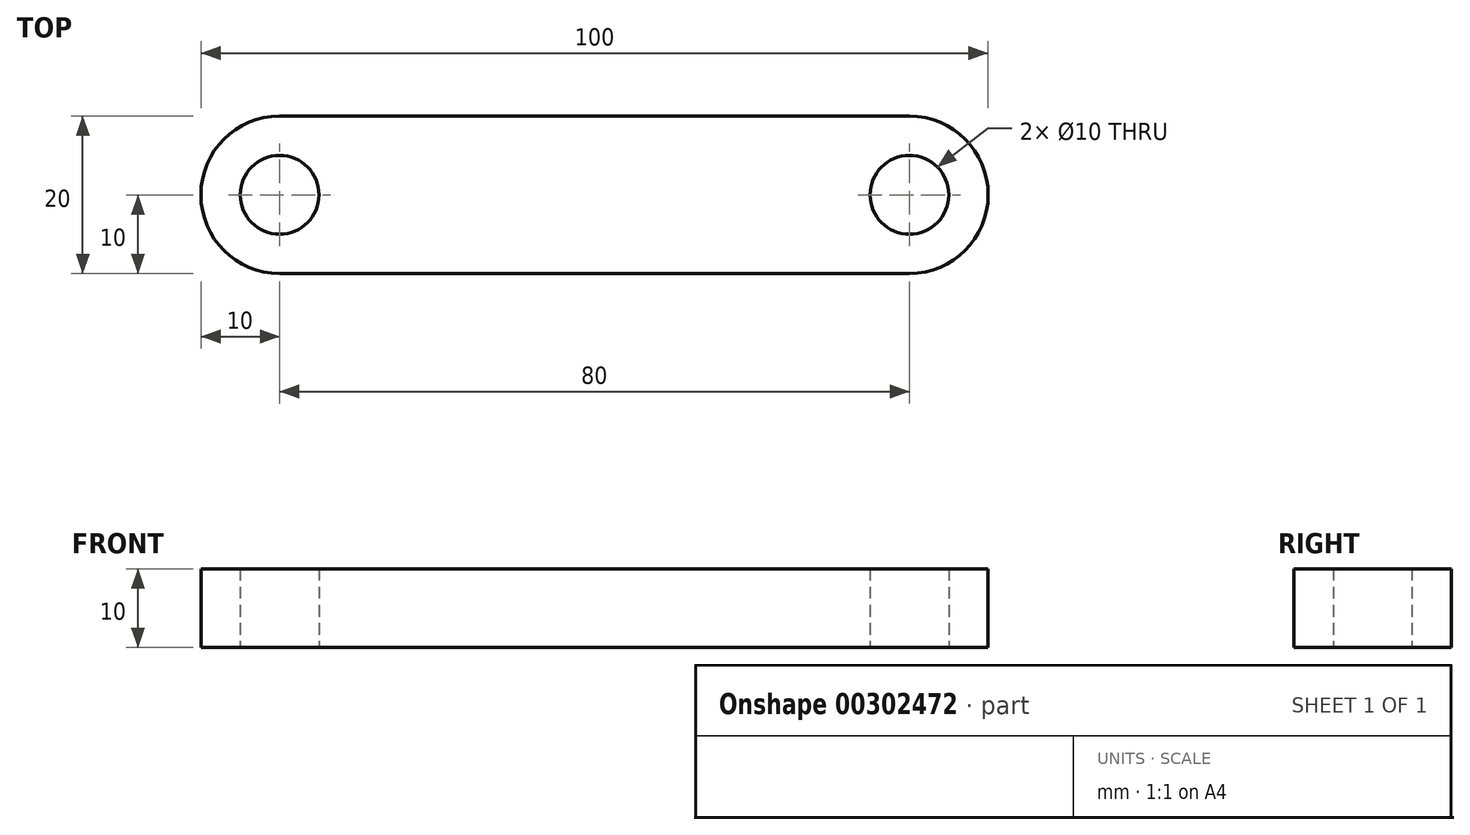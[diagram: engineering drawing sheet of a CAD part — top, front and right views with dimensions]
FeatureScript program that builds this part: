
annotation { "Feature Type Name" : "Feature", "Feature Type Description" : "" }
export const myFeature = defineFeature(function(context is Context, id is Id, definition is map)
    precondition{}
    {
        {
            var Q0;
            Q0=qCreatedBy(makeId("Top.planeOp"),FACE);
            var sketch = newSketch(context, id + "F0", { "sketchPlane" : qUnion([Q0])});
            skLineSegment(sketch, "E0", {"start": v(0, 0) * mm, "end": v(80, 0) * mm, "construction": true});
            skArc(sketch, "E1.0.startCap", {"start": v(0, -10) * mm, "mid": v(-10, 0) * mm, "end": v(0, 10) * mm});
            skArc(sketch, "E1.0.endCap", {"start": v(80, 10) * mm, "mid": v(90, 0) * mm, "end": v(80, -10) * mm});
            skLineSegment(sketch, "E1.0.left", {"start": v(0, 10) * mm, "end": v(80, 10) * mm});
            skLineSegment(sketch, "E1.0.right", {"start": v(0, -10) * mm, "end": v(80, -10) * mm});
            skCircle(sketch, "E2", {"center": v(0, 0) * mm, "radius": 5 * mm});
            skCircle(sketch, "E3", {"center": v(80, 0) * mm, "radius": 5 * mm});
            skSolve(sketch);
        }
        {
            var Q0;
            Q0 = qSketchRegion(id + "F0", true);
            extrude(context, id + "F1", {"entities" : qUnion([Q0]), "depth" : 10 * mm});
        }
    });
